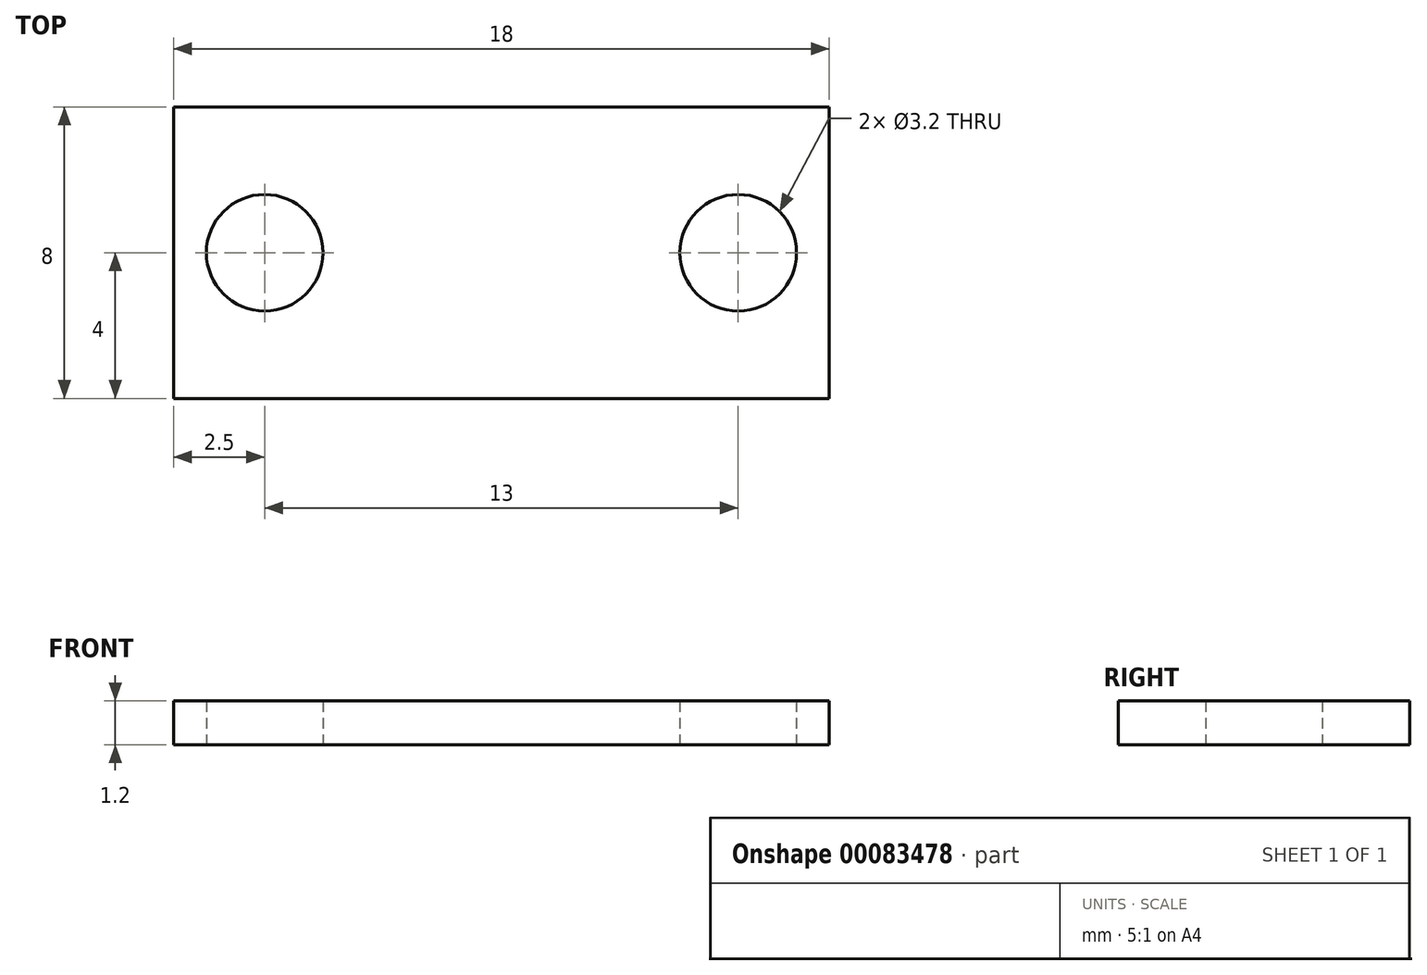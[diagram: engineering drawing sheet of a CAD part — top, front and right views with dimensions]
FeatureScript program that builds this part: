
annotation { "Feature Type Name" : "Feature", "Feature Type Description" : "" }
export const myFeature = defineFeature(function(context is Context, id is Id, definition is map)
    precondition{}
    {
        {
            var Q0;
            Q0=qCreatedBy(makeId("Top.planeOp"),FACE);
            var sketch = newSketch(context, id + "F0", { "sketchPlane" : qUnion([Q0])});
            skLineSegment(sketch, "E0.bottom", {"start": v(0, 0) * mm, "end": v(18, 0) * mm});
            skLineSegment(sketch, "E0.top", {"start": v(0, 8) * mm, "end": v(18, 8) * mm});
            skLineSegment(sketch, "E0.left", {"start": v(0, 0) * mm, "end": v(0, 8) * mm});
            skLineSegment(sketch, "E0.right", {"start": v(18, 0) * mm, "end": v(18, 8) * mm});
            skCircle(sketch, "E1", {"center": v(2.5, 4) * mm, "radius": 1.6 * mm});
            skCircle(sketch, "E2", {"center": v(15.5, 4) * mm, "radius": 1.6 * mm});
            skSolve(sketch);
        }
        {
            var Q0;
            Q0=qSketchRegion(id+"F0",true);
            extrude(context, id + "F1", {"entities" : qUnion([Q0]), "depth" : 1.2 * mm});
        }
    });
